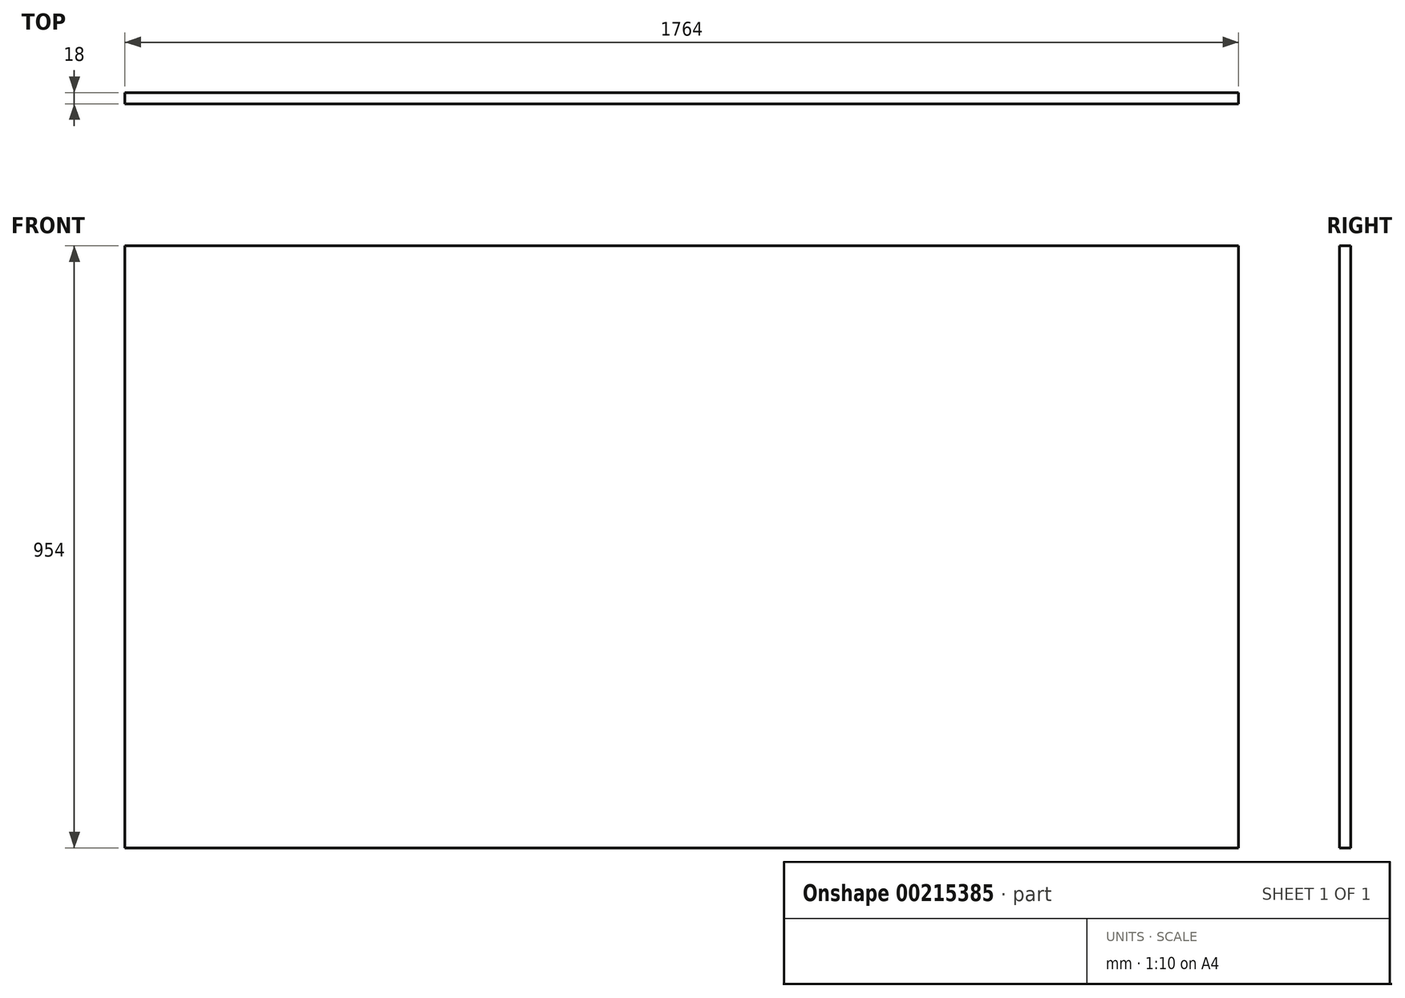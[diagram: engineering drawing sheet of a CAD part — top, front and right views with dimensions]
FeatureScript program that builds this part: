
annotation { "Feature Type Name" : "Feature", "Feature Type Description" : "" }
export const myFeature = defineFeature(function(context is Context, id is Id, definition is map)
    precondition{}
    {
        {
            var Q0;
            Q0=qCreatedBy(makeId("Front.planeOp"),FACE);
            var sketch = newSketch(context, id + "F0", { "sketchPlane" : qUnion([Q0])});
            skLineSegment(sketch, "E0.bottom", {"start": v(-882, -477) * mm, "end": v(882, -477) * mm});
            skLineSegment(sketch, "E0.top", {"start": v(-882, 477) * mm, "end": v(882, 477) * mm});
            skLineSegment(sketch, "E0.left", {"start": v(-882, -477) * mm, "end": v(-882, 477) * mm});
            skLineSegment(sketch, "E0.right", {"start": v(882, -477) * mm, "end": v(882, 477) * mm});
            skPoint(sketch, "E0.middle", {"position": v(0, 0) * mm});
            skSolve(sketch);
        }
        {
            var Q0;
            Q0=makeQuery(id+"F0.imprint","IMPRINT",FACE,{"disambiguationData":[TD([[makeQuery(id+"F0.imprint","IMPRINT",EDGE,{"derivedFrom":sQuery(id+"F0.wireOp",EDGE,"E0.bottom")}),1.0]])]});
            extrude(context, id + "F1", {"entities" : qUnion([Q0]), "depth" : 18 * mm});
        }
    });
